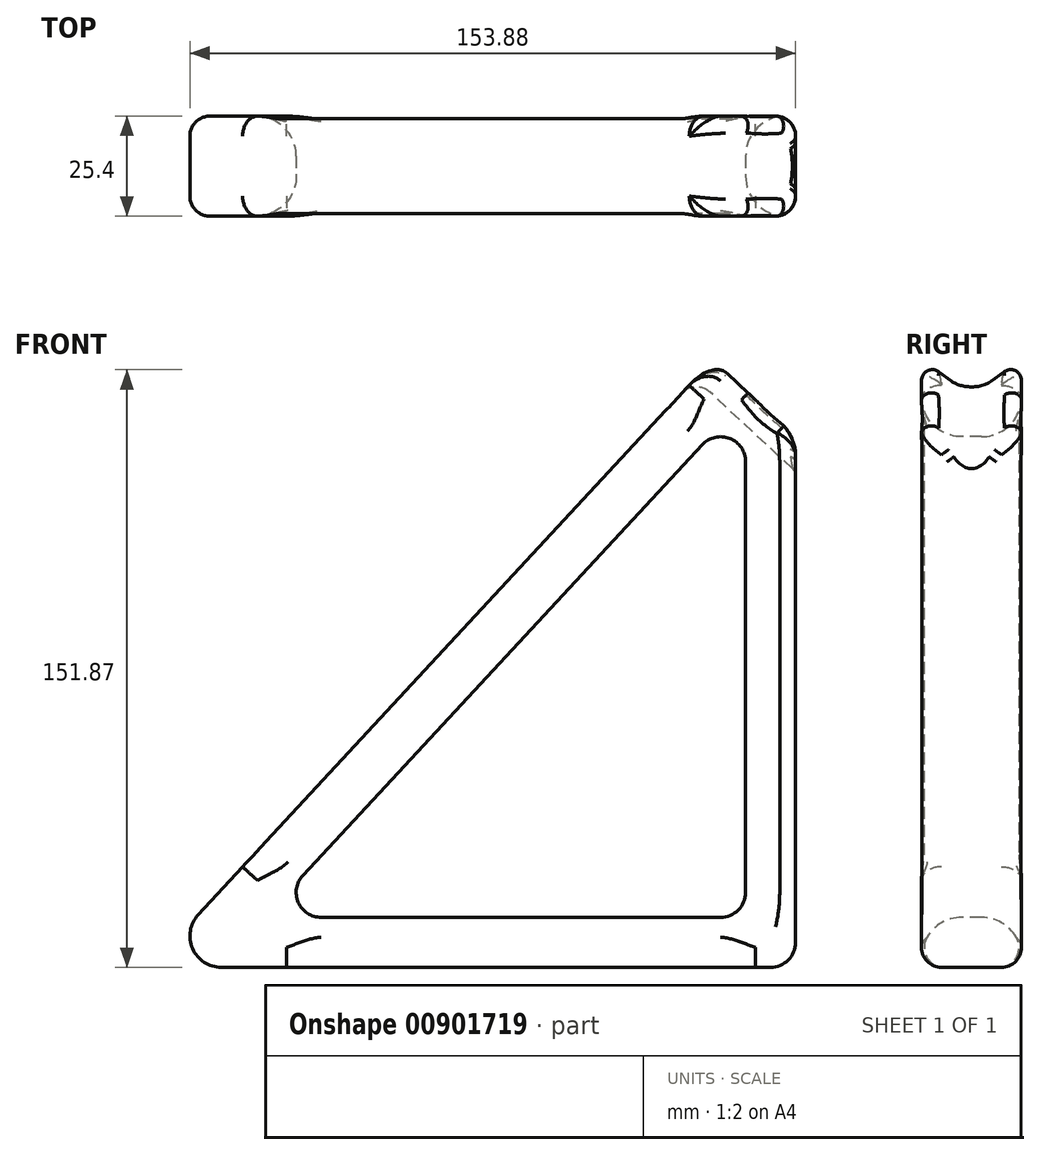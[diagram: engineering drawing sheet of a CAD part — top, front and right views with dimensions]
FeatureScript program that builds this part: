
annotation { "Feature Type Name" : "Feature", "Feature Type Description" : "" }
export const myFeature = defineFeature(function(context is Context, id is Id, definition is map)
    precondition{}
    {
        {
            var Q0;
            Q0=qCreatedBy(makeId("Front.planeOp"),FACE);
            var sketch = newSketch(context, id + "F0", { "sketchPlane" : qUnion([Q0])});
            skLineSegment(sketch, "E0.bottom", {"start": v(-6.35, 0) * mm, "end": v(-145.91, 0) * mm});
            skLineSegment(sketch, "E0.top", {"start": v(0, 139.7) * mm, "end": v(-17.96, 157.66) * mm});
            skLineSegment(sketch, "E0.left", {"start": v(0, 6.35) * mm, "end": v(0, 139.7) * mm});
            skLineSegment(sketch, "E1", {"start": v(-17.96, 157.66) * mm, "end": v(-151.76, 13.4) * mm});
            skLineSegment(sketch, "E2", {"start": v(-125.19, 23.37) * mm, "end": v(-23.7, 132.79) * mm});
            skLineSegment(sketch, "E3", {"start": v(-12.7, 128.47) * mm, "end": v(-12.7, 19.05) * mm});
            skLineSegment(sketch, "E4", {"start": v(-19.05, 12.7) * mm, "end": v(-120.53, 12.7) * mm});
            skArc(sketch, "E5.filletArc", {"start": v(-125.19, 23.37) * mm, "mid": v(-126.35, 16.5) * mm, "end": v(-120.53, 12.7) * mm});
            skPoint(sketch, "E6.visualSharp", {"position": v(-12.7, 12.7) * mm});
            skArc(sketch, "E6.filletArc", {"start": v(-19.05, 12.7) * mm, "mid": v(-14.56, 14.56) * mm, "end": v(-12.7, 19.05) * mm});
            skPoint(sketch, "E7.visualSharp", {"position": v(0, 0) * mm});
            skArc(sketch, "E7.filletArc", {"start": v(-6.35, 0) * mm, "mid": v(-1.86, 1.86) * mm, "end": v(0, 6.35) * mm});
            skArc(sketch, "E8.filletArc", {"start": v(-12.7, 128.47) * mm, "mid": v(-16.73, 134.38) * mm, "end": v(-23.7, 132.79) * mm});
            skPoint(sketch, "E9.visualSharp", {"position": v(0, 139.7) * mm});
            skPoint(sketch, "E10.visualSharp", {"position": v(-17.96, 157.66) * mm});
            skArc(sketch, "E11", {"start": v(-151.76, 13.4) * mm, "mid": v(-153.22, 4.78) * mm, "end": v(-145.91, 0) * mm});
            skSolve(sketch);
        }
        {
            var Q0;
            Q0=makeQuery(id+"F0.imprint","IMPRINT",FACE,{"disambiguationData":[TD([[makeQuery(id+"F0.imprint","IMPRINT",EDGE,{"derivedFrom":sQuery(id+"F0.wireOp",EDGE,"E0.bottom")}),-1.0]])]});
            extrude(context, id + "F1", {"entities" : qUnion([Q0]), "oppositeDirection" : true, "depth" : 25.4 * mm, "offsetDistance" : 25.4 * mm, "symmetric" : true});
        }
        {
            var Q0;
            Q0=makeQuery(id+"F1.opExtrude","SWEPT_FACE",FACE,{"disambiguationData":[OSD([sQuery(id+"F0.wireOp",EDGE,"E1")])]});
            var sketch = newSketch(context, id + "F2", { "sketchPlane" : qUnion([Q0])});
            skLineSegment(sketch, "E12", {"start": v(12.7, 102.43) * mm, "end": v(4.5, 94.22) * mm});
            skLineSegment(sketch, "E13", {"start": v(-4.5, 94.22) * mm, "end": v(-12.7, 102.43) * mm});
            skPoint(sketch, "E14.visualSharp", {"position": v(0, 89.73) * mm});
            skArc(sketch, "E14.filletArc", {"start": v(-4.5, 94.22) * mm, "mid": v(0, 92.36) * mm, "end": v(4.5, 94.22) * mm});
            skLineSegment(sketch, "E15.0", {"start": v(12.7, 102.43) * mm, "end": v(-12.7, 102.43) * mm});
            skSolve(sketch);
        }
        {
            var Q0;
            {var subQ0=sQuery(id+"F2.wireOp",EDGE,"E15.0");Q0=makeQuery(id+"F2.imprint","IMPRINT",FACE,{"disambiguationData":[TD([[makeQuery(id+"F2.imprint","IMPRINT",EDGE,{"derivedFrom":subQ0}),-1.0]])]});}
            var Q1;
            {var subQ0=sQuery(id+"F2.wireOp",EDGE,"E14.filletArc");Q1=makeQuery(id+"F2.imprint","IMPRINT",FACE,{"disambiguationData":[TD([[makeQuery(id+"F2.imprint","IMPRINT",EDGE,{"derivedFrom":subQ0}),1.0]])]});}
            extrude(context, id + "F3", {"entities" : qUnion([Q0, Q1]), "operationType" : NewBodyOperationType.REMOVE, "endBound" : BoundingType.THROUGH_ALL, "oppositeDirection" : true, "depth" : 25.4 * mm, "offsetDistance" : 25.4 * mm});
        }
        {
            var Q0;
            Q0=makeQuery(id+"F1.opExtrude","SWEPT_FACE",FACE,{"disambiguationData":[OSD([sQuery(id+"F0.wireOp",EDGE,"E4")])]});
            fillet(context, id + "F4", {"entities" : qUnion([Q0]), "radius" : 10.16 * mm, "tangentPropagation" : true, "allowEdgeOverflow" : false});
        }
        {
            var Q0;
            Q0=makeQuery(id+"F1.opExtrude","SWEPT_FACE",FACE,{"disambiguationData":[OSD([sQuery(id+"F0.wireOp",EDGE,"E1")])]});
            fillet(context, id + "F5", {"entities" : qUnion([Q0]), "radius" : 5.08 * mm, "tangentPropagation" : true, "allowEdgeOverflow" : false});
        }
        {
            var Q0;
            Q0=makeQuery(id+"F3.boolean.opBoolean","INTERSECT",EDGE,{"derivedFrom":[makeQuery(id+"F1.opExtrude","SWEPT_FACE",FACE,{"disambiguationData":[OSD([sQuery(id+"F0.wireOp",EDGE,"E0.left")])]}),makeQuery(id+"F3.opExtrude","SWEPT_FACE",FACE,{"disambiguationData":[OSD([sQuery(id+"F2.wireOp",EDGE,"E14.filletArc")])]})]});
            var Q1;
            Q1=makeQuery(id+"F3.boolean.opBoolean","INTERSECT",EDGE,{"derivedFrom":[makeQuery(id+"F1.opExtrude","SWEPT_FACE",FACE,{"disambiguationData":[OSD([sQuery(id+"F0.wireOp",EDGE,"E0.left")])]}),makeQuery(id+"F3.opExtrude","SWEPT_FACE",FACE,{"disambiguationData":[OSD([sQuery(id+"F2.wireOp",EDGE,"E12")])]})]});
            var Q2;
            Q2=makeQuery(id+"F3.boolean.opBoolean","INTERSECT",EDGE,{"derivedFrom":[makeQuery(id+"F1.opExtrude","SWEPT_FACE",FACE,{"disambiguationData":[OSD([sQuery(id+"F0.wireOp",EDGE,"E0.left")])]}),makeQuery(id+"F3.opExtrude","SWEPT_FACE",FACE,{"disambiguationData":[OSD([sQuery(id+"F2.wireOp",EDGE,"E13")])]})]});
            fillet(context, id + "F6", {"entities" : qUnion([Q0, Q1, Q2]), "radius" : 2.54 * mm, "tangentPropagation" : true, "allowEdgeOverflow" : false});
        }
    });
